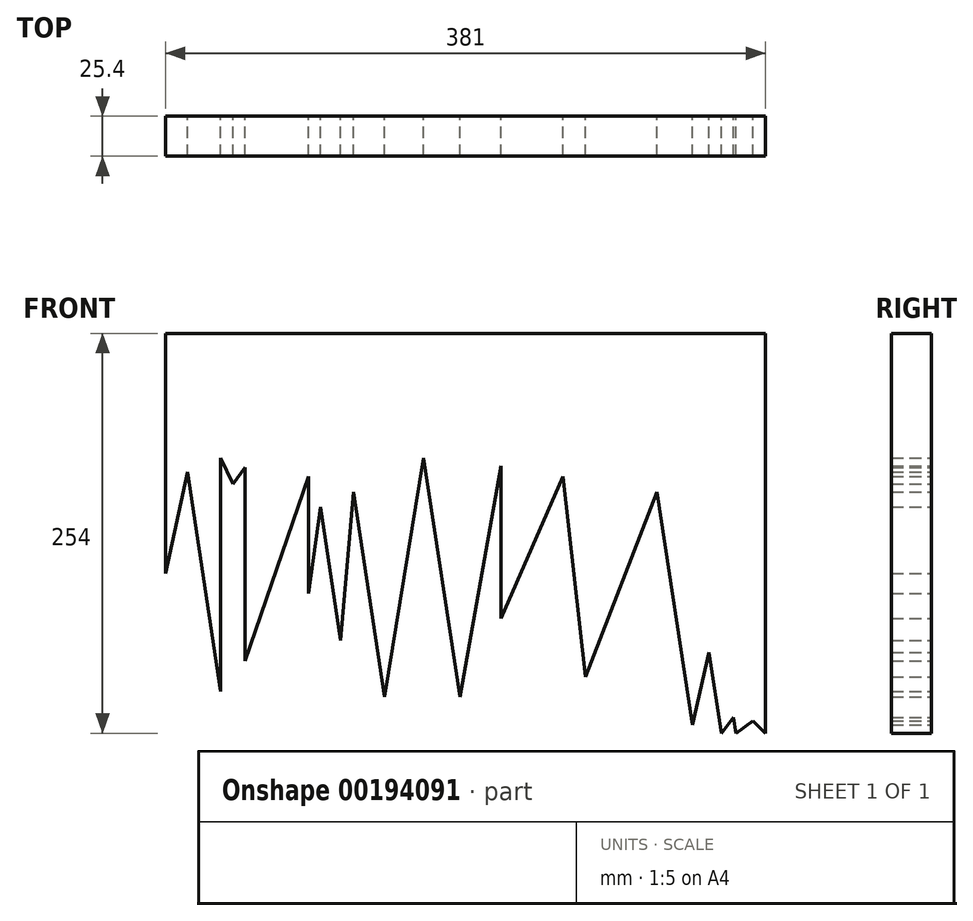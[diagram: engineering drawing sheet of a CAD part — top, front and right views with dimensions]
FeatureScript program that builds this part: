
annotation { "Feature Type Name" : "Feature", "Feature Type Description" : "" }
export const myFeature = defineFeature(function(context is Context, id is Id, definition is map)
    precondition{}
    {
        {
            var Q0;
            Q0=qCreatedBy(makeId("Front.planeOp"),FACE);
            var sketch = newSketch(context, id + "F0", { "sketchPlane" : qUnion([Q0])});
            skLineSegment(sketch, "E0", {"start": v(-199.22, 0) * mm, "end": v(181.78, 0) * mm});
            skLineSegment(sketch, "E1", {"start": v(181.78, 0) * mm, "end": v(181.78, -254) * mm});
            skLineSegment(sketch, "E2", {"start": v(-199.22, 0) * mm, "end": v(-199.22, -152.4) * mm});
            skLineSegment(sketch, "E3", {"start": v(-199.22, -152.4) * mm, "end": v(-185.32, -88.18) * mm});
            skLineSegment(sketch, "E4", {"start": v(-185.32, -88.18) * mm, "end": v(-164.22, -227.33) * mm});
            skLineSegment(sketch, "E5", {"start": v(-164.22, -227.33) * mm, "end": v(-164.22, -79.06) * mm});
            skLineSegment(sketch, "E6", {"start": v(-164.22, -79.06) * mm, "end": v(-156.23, -95.6) * mm});
            skLineSegment(sketch, "E7", {"start": v(-156.23, -95.6) * mm, "end": v(-148.82, -85.33) * mm});
            skLineSegment(sketch, "E8", {"start": v(-148.82, -85.33) * mm, "end": v(-148.82, -207.94) * mm});
            skLineSegment(sketch, "E9", {"start": v(-148.82, -207.94) * mm, "end": v(-108.33, -91.03) * mm});
            skLineSegment(sketch, "E10", {"start": v(-108.33, -91.03) * mm, "end": v(-108.33, -165.17) * mm});
            skLineSegment(sketch, "E11", {"start": v(-108.33, -165.17) * mm, "end": v(-100.91, -110.42) * mm});
            skLineSegment(sketch, "E12", {"start": v(-100.91, -110.42) * mm, "end": v(-88.06, -195.18) * mm});
            skLineSegment(sketch, "E13", {"start": v(-88.06, -195.18) * mm, "end": v(-79.81, -100.73) * mm});
            skLineSegment(sketch, "E14", {"start": v(-79.81, -100.73) * mm, "end": v(-60.1, -230.79) * mm});
            skLineSegment(sketch, "E15", {"start": v(-60.1, -230.79) * mm, "end": v(-35.33, -79.06) * mm});
            skLineSegment(sketch, "E16", {"start": v(-35.33, -79.06) * mm, "end": v(-12.32, -230.79) * mm});
            skLineSegment(sketch, "E17", {"start": v(-12.32, -230.79) * mm, "end": v(13.71, -84.2) * mm});
            skLineSegment(sketch, "E18", {"start": v(13.71, -84.2) * mm, "end": v(13.71, -181.14) * mm});
            skLineSegment(sketch, "E19", {"start": v(13.71, -181.14) * mm, "end": v(53.06, -91.03) * mm});
            skLineSegment(sketch, "E20", {"start": v(53.06, -91.03) * mm, "end": v(67.32, -218.2) * mm});
            skLineSegment(sketch, "E21", {"start": v(67.32, -218.2) * mm, "end": v(112.94, -100.73) * mm});
            skLineSegment(sketch, "E22", {"start": v(112.94, -100.73) * mm, "end": v(135.4, -248.83) * mm});
            skLineSegment(sketch, "E23", {"start": v(135.4, -248.83) * mm, "end": v(146.02, -202.8) * mm});
            skLineSegment(sketch, "E24", {"start": v(146.02, -202.8) * mm, "end": v(153.78, -254) * mm});
            skLineSegment(sketch, "E25", {"start": v(153.78, -254) * mm, "end": v(161.42, -243.87) * mm});
            skLineSegment(sketch, "E26", {"start": v(161.42, -243.87) * mm, "end": v(162.95, -254) * mm});
            skLineSegment(sketch, "E27", {"start": v(162.95, -254) * mm, "end": v(173.96, -246.15) * mm});
            skLineSegment(sketch, "E28", {"start": v(173.96, -246.15) * mm, "end": v(181.78, -254) * mm});
            skSolve(sketch);
        }
        {
            var Q0;
            Q0 = qSketchRegion(id + "F0", true);
            extrude(context, id + "F1", {"entities" : qUnion([Q0]), "depth" : 12.7 * mm});
        }
        {
            var Q0;
            Q0 = qSketchRegion(id + "F0", true);
            extrude(context, id + "F2", {"entities" : qUnion([Q0]), "operationType" : NewBodyOperationType.ADD, "depth" : 25.4 * mm});
        }
    });
